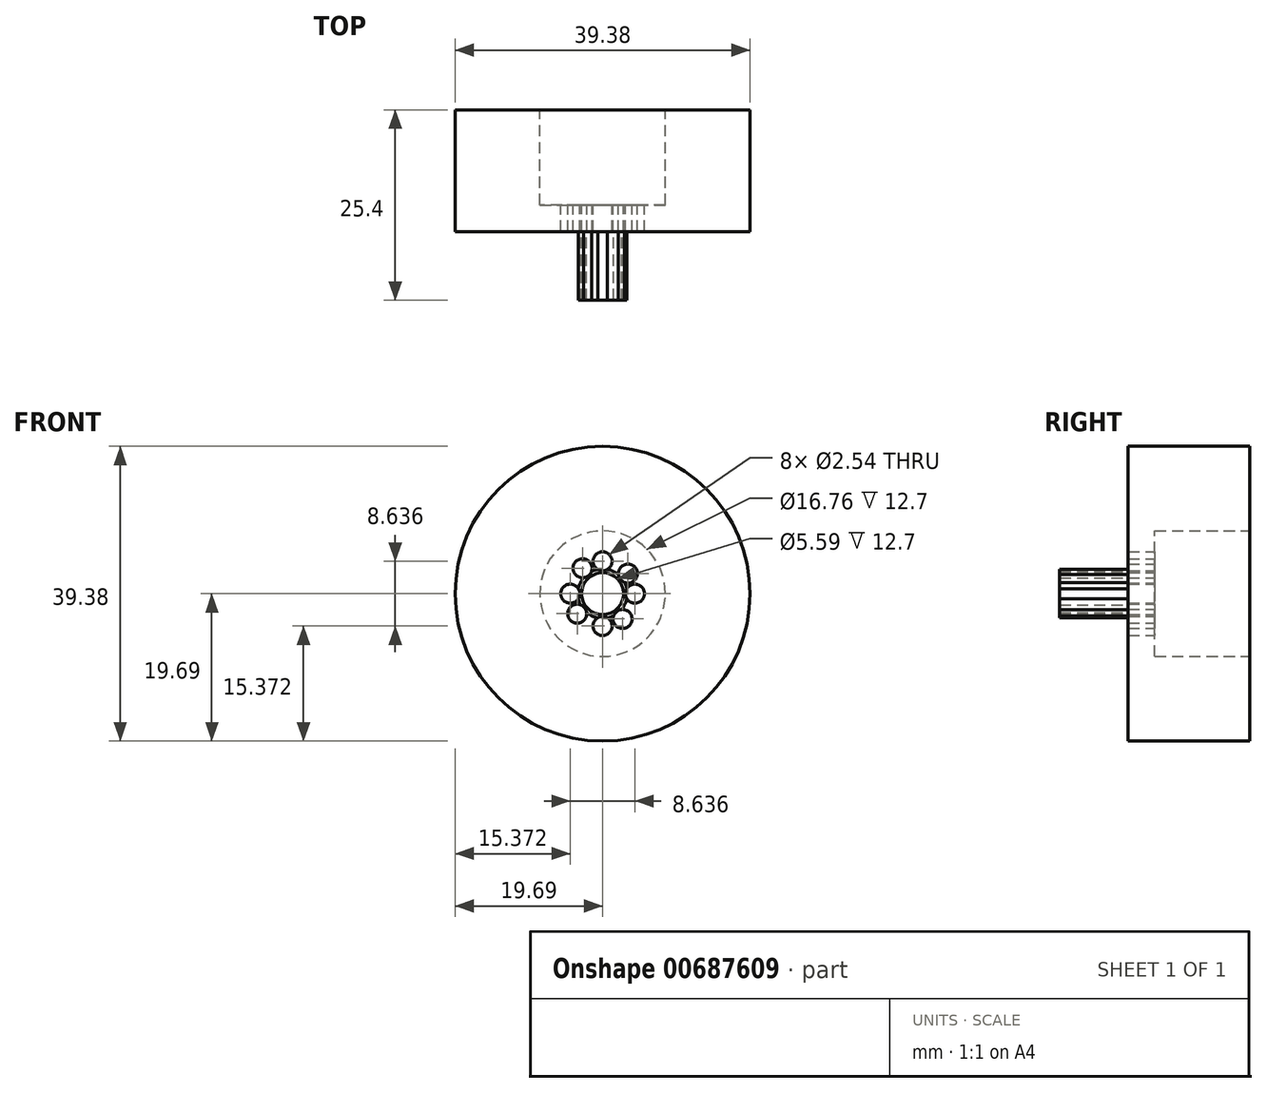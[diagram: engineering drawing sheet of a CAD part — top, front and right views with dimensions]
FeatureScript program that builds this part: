
annotation { "Feature Type Name" : "Feature", "Feature Type Description" : "" }
export const myFeature = defineFeature(function(context is Context, id is Id, definition is map)
    precondition{}
    {
        {
            var Q0;
            Q0=qCreatedBy(makeId("Front.planeOp"),FACE);
            var sketch = newSketch(context, id + "F0", { "sketchPlane" : qUnion([Q0])});
            skCircle(sketch, "E0", {"center": v(0, 0) * mm, "radius": 19.69 * mm});
            skSolve(sketch);
        }
        {
            var Q0;
            Q0 = qSketchRegion(id + "FVOFRWJk0czvBla_0", true);
            var Q1;
            Q1=makeQuery(id+"F0.imprint","IMPRINT",FACE,{"disambiguationData":[TD([[makeQuery(id+"F0.imprint","IMPRINT",EDGE,{"derivedFrom":sQuery(id+"F0.wireOp",EDGE,"E0")}),1.0]])]});
            extrude(context, id + "F1", {"entities" : qUnion([Q0, Q1]), "depth" : 16.26 * mm, "offsetDistance" : 25.4 * mm});
        }
        {
            var Q0;
            Q0=qCreatedBy(makeId("Front.planeOp"),FACE);
            var sketch = newSketch(context, id + "F2", { "sketchPlane" : qUnion([Q0])});
            skCircle(sketch, "E1", {"center": v(0, 0) * mm, "radius": 8.38 * mm});
            skSolve(sketch);
        }
        {
            var Q0;
            Q0=makeQuery(id+"F2.imprint","IMPRINT",FACE,{"disambiguationData":[TD([[makeQuery(id+"F2.imprint","IMPRINT",EDGE,{"derivedFrom":sQuery(id+"F2.wireOp",EDGE,"E1")}),1.0]])]});
            extrude(context, id + "F3", {"entities" : qUnion([Q0]), "operationType" : NewBodyOperationType.REMOVE, "depth" : 12.7 * mm, "offsetDistance" : 25.4 * mm});
        }
        {
            var Q0;
            Q0=makeQuery(id+"F1.opExtrude","CAP_FACE",FACE,{"disambiguationData":[OSD([sQuery(id+"F0.wireOp",EDGE,"E0")])],"isStart":false});
            var sketch = newSketch(context, id + "F4", { "sketchPlane" : qUnion([Q0])});
            skCircle(sketch, "E2", {"center": v(0, 0) * mm, "radius": 3.3 * mm});
            skSolve(sketch);
        }
        {
            var Q0;
            Q0 = qSketchRegion(id + "F4", true);
            extrude(context, id + "F5", {"entities" : qUnion([Q0]), "operationType" : NewBodyOperationType.ADD, "depth" : 9.14 * mm, "offsetDistance" : 25.4 * mm});
        }
        {
            var Q0;
            Q0=qCreatedBy(makeId("Front.planeOp"),FACE);
            var sketch = newSketch(context, id + "F6", { "sketchPlane" : qUnion([Q0])});
            skLineSegment(sketch, "E3", {"start": v(0, 0) * mm, "end": v(2.67, -3.38) * mm});
            skLineSegment(sketch, "E4", {"start": v(2.67, -3.38) * mm, "end": v(0, 0) * mm});
            skLineSegment(sketch, "E5", {"start": v(0, 0) * mm, "end": v(-3.39, -2.68) * mm});
            skLineSegment(sketch, "E6", {"start": v(0, 0) * mm, "end": v(-2.68, 3.39) * mm});
            skLineSegment(sketch, "E7", {"start": v(-2.68, 3.39) * mm, "end": v(0, 0) * mm});
            skLineSegment(sketch, "E8", {"start": v(0, 0) * mm, "end": v(-4.32, 0) * mm});
            skLineSegment(sketch, "E9", {"start": v(-4.32, 0) * mm, "end": v(0, 0) * mm});
            skLineSegment(sketch, "E10", {"start": v(0, 0) * mm, "end": v(4.32, 0) * mm});
            skLineSegment(sketch, "E11", {"start": v(4.32, 0) * mm, "end": v(0, 0) * mm});
            skLineSegment(sketch, "E12", {"start": v(0, 0) * mm, "end": v(3.39, 2.68) * mm});
            skLineSegment(sketch, "E13", {"start": v(3.39, 2.68) * mm, "end": v(0, 0) * mm});
            skLineSegment(sketch, "E14", {"start": v(0, 0) * mm, "end": v(0, 4.32) * mm});
            skLineSegment(sketch, "E15", {"start": v(0, 0) * mm, "end": v(0, -4.32) * mm});
            skCircle(sketch, "E16", {"center": v(0, -4.32) * mm, "radius": 1.27 * mm});
            skCircle(sketch, "E17", {"center": v(-3.39, -2.68) * mm, "radius": 1.27 * mm});
            skCircle(sketch, "E18", {"center": v(-4.32, 0) * mm, "radius": 1.27 * mm});
            skCircle(sketch, "E19", {"center": v(-2.68, 3.39) * mm, "radius": 1.27 * mm});
            skCircle(sketch, "E20", {"center": v(0, 4.32) * mm, "radius": 1.27 * mm});
            skCircle(sketch, "E21", {"center": v(3.39, 2.68) * mm, "radius": 1.27 * mm});
            skCircle(sketch, "E22", {"center": v(4.32, 0) * mm, "radius": 1.27 * mm});
            skCircle(sketch, "E23", {"center": v(2.67, -3.38) * mm, "radius": 1.27 * mm});
            skSolve(sketch);
        }
        {
            var Q0;
            Q0=makeQuery(id+"F6.imprint","IMPRINT",FACE,{"disambiguationData":[TD([[makeQuery(id+"F6.imprint","IMPRINT",EDGE,{"derivedFrom":sQuery(id+"F6.wireOp",EDGE,"E20")}),1.0]])]});
            var Q1;
            Q1=makeQuery(id+"F6.imprint","IMPRINT",FACE,{"disambiguationData":[TD([[makeQuery(id+"F6.imprint","IMPRINT",EDGE,{"derivedFrom":sQuery(id+"F6.wireOp",EDGE,"E19")}),1.0]])]});
            var Q2;
            Q2=makeQuery(id+"F6.imprint","IMPRINT",FACE,{"disambiguationData":[TD([[makeQuery(id+"F6.imprint","IMPRINT",EDGE,{"derivedFrom":sQuery(id+"F6.wireOp",EDGE,"E18")}),1.0]])]});
            var Q3;
            Q3=makeQuery(id+"F6.imprint","IMPRINT",FACE,{"disambiguationData":[TD([[makeQuery(id+"F6.imprint","IMPRINT",EDGE,{"derivedFrom":sQuery(id+"F6.wireOp",EDGE,"E17")}),1.0]])]});
            var Q4;
            Q4=makeQuery(id+"F6.imprint","IMPRINT",FACE,{"disambiguationData":[TD([[makeQuery(id+"F6.imprint","IMPRINT",EDGE,{"derivedFrom":sQuery(id+"F6.wireOp",EDGE,"E16")}),1.0]])]});
            var Q5;
            Q5=makeQuery(id+"F6.imprint","IMPRINT",FACE,{"disambiguationData":[TD([[makeQuery(id+"F6.imprint","IMPRINT",EDGE,{"derivedFrom":sQuery(id+"F6.wireOp",EDGE,"E23")}),1.0]])]});
            var Q6;
            Q6=makeQuery(id+"F6.imprint","IMPRINT",FACE,{"disambiguationData":[TD([[makeQuery(id+"F6.imprint","IMPRINT",EDGE,{"derivedFrom":sQuery(id+"F6.wireOp",EDGE,"E22")}),1.0]])]});
            var Q7;
            Q7=makeQuery(id+"F6.imprint","IMPRINT",FACE,{"disambiguationData":[TD([[makeQuery(id+"F6.imprint","IMPRINT",EDGE,{"derivedFrom":sQuery(id+"F6.wireOp",EDGE,"E21")}),1.0]])]});
            extrude(context, id + "F7", {"entities" : qUnion([Q0, Q1, Q2, Q3, Q4, Q5, Q6, Q7]), "operationType" : NewBodyOperationType.REMOVE, "depth" : 25.4 * mm, "offsetDistance" : 25.4 * mm});
        }
        {
            var Q0;
            Q0=makeQuery(id+"F3.boolean.opBoolean","COPY",FACE,{"derivedFrom":makeQuery(id+"F3.opExtrude","CAP_FACE",FACE,{"disambiguationData":[OSD([sQuery(id+"F2.wireOp",EDGE,"E1")])],"isStart":false})});
            var sketch = newSketch(context, id + "F8", { "sketchPlane" : qUnion([Q0])});
            skCircle(sketch, "E24", {"center": v(0, 0) * mm, "radius": 2.8 * mm});
            skSolve(sketch);
        }
        {
            var Q0;
            Q0=makeQuery(id+"F8.imprint","IMPRINT",FACE,{"disambiguationData":[TD([[makeQuery(id+"F8.imprint","IMPRINT",EDGE,{"derivedFrom":sQuery(id+"F8.wireOp",EDGE,"E24")}),1.0]])]});
            extrude(context, id + "F9", {"entities" : qUnion([Q0]), "operationType" : NewBodyOperationType.REMOVE, "oppositeDirection" : true, "depth" : 25.4 * mm, "offsetDistance" : 25.4 * mm});
        }
    });
